# Revit family: Casual_Space_Division-Teknion-HNBTSS_Navigate_Single_Sided_End_of_Run_Screen_Solid-R2016
name_source: partatom
category: Furniture
revit_build: Autodesk Revit Architecture 2016 (Build: 20190507_1515(x64)
units: mm (PartAtom-declared; Revit-internal decimal feet)

## family parameters
Always vertical = Yes
Cut with Voids When Loaded = No
OmniClass Number = 23.40.20.00
OmniClass Title = General Furniture and Specialties
Room Calculation Point = No
Shared = Yes
Work Plane-Based = No

## types (4) — shared parameters
Assembly Code = E2020200
Manufacturer = Teknion
Manufacturer Fax = 416.661.4586
Part Number = HNBTSS
Product Documentation Link = https://www.teknion.com
Product Line = Navigate Height-Adjustable Bench
Product Page URL = https://www.teknion.com
Series = Navigate Height-Adjustable Bench
Sustainability Data = https://www.teknion.com
URL = www.teknion.com
Unit Weight URL = http://www.teknion.com
Warranty = http://www.teknion.com

## per-type parameters (varying)
| type | Description | Height | Model | Width |
| 42"h x 24"w | Navigate Single-Sided End of Run Screen – Solid, 42" Height, 24" Width | 41.575 " | HNBTSS4224_ | 31 " |
| 42"h x 30"w | Navigate Single-Sided End of Run Screen – Solid, 42" Height, 30" Width | 41.575 " | HNBTSS4230_ | 37 " |
| 51"h x 30"w | Navigate Single-Sided End of Run Screen – Solid, 51" Height, 30" Width | 50.575 " | HNBTSS5130_ | 37 " |
| 51"h x 24"w | Navigate Single-Sided End of Run Screen – Solid, 51" Height, 24" Width | 50.575 " | HNBTSS5124_ | 31 " |

## geometry (parser evidence)
native form markers: Sweep x2
no freeform markers — native parametric forms only
